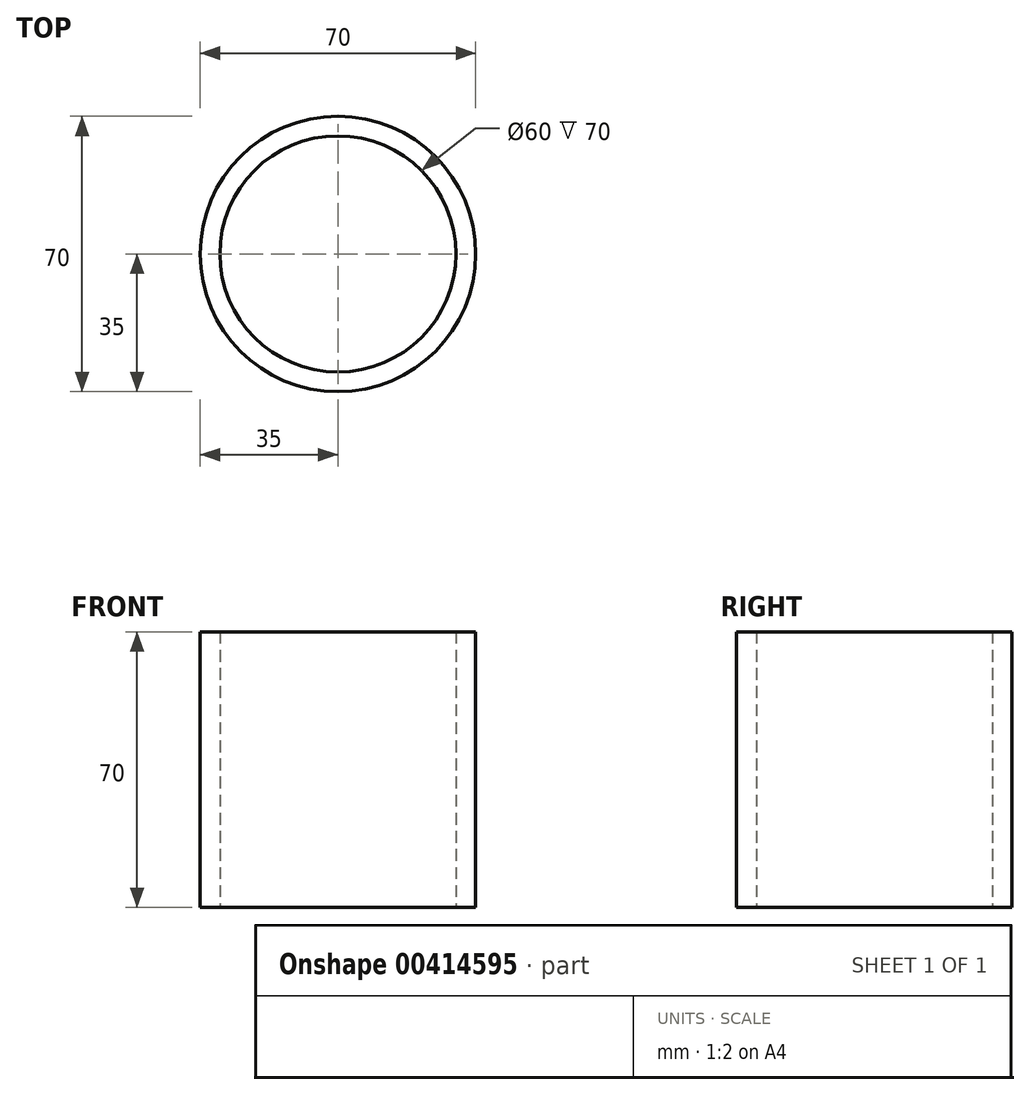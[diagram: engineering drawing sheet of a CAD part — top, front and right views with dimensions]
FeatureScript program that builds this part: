
annotation { "Feature Type Name" : "Feature", "Feature Type Description" : "" }
export const myFeature = defineFeature(function(context is Context, id is Id, definition is map)
    precondition{}
    {
        {
            var Q0;
            Q0=qCreatedBy(makeId("Top.planeOp"),FACE);
            var sketch = newSketch(context, id + "F0", { "sketchPlane" : qUnion([Q0])});
            skCircle(sketch, "E0", {"center": v(0, 0) * mm, "radius": 35 * mm});
            skCircle(sketch, "E1", {"center": v(0, 0) * mm, "radius": 30 * mm});
            skSolve(sketch);
        }
        {
            var Q0;
            Q0 = qSketchRegion(id + "F0", true);
            extrude(context, id + "F1", {"entities" : qUnion([Q0]), "depth" : 70 * mm});
        }
    });
